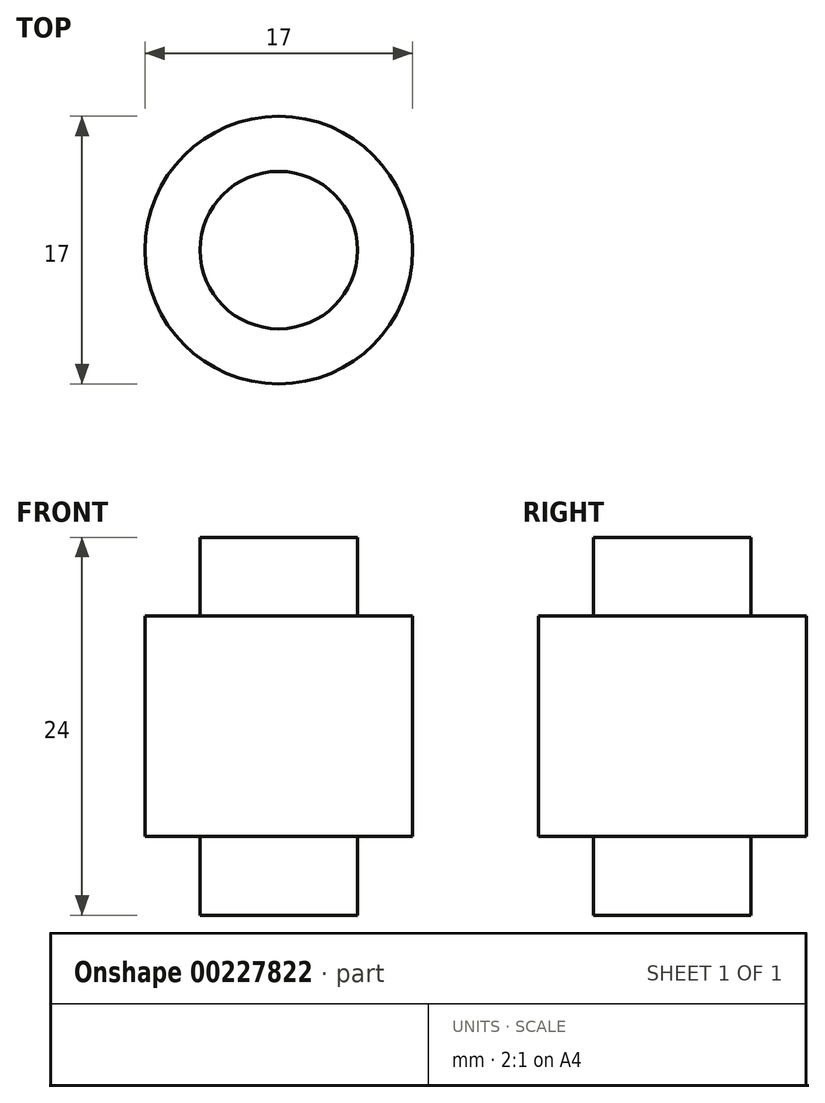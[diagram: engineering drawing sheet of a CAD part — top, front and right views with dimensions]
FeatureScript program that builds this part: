
annotation { "Feature Type Name" : "Feature", "Feature Type Description" : "" }
export const myFeature = defineFeature(function(context is Context, id is Id, definition is map)
    precondition{}
    {
        {
            var Q0;
            Q0=qCreatedBy(makeId("Front.planeOp"),FACE);
            var sketch = newSketch(context, id + "F0", { "sketchPlane" : qUnion([Q0])});
            skLineSegment(sketch, "E0", {"start": v(0, 12) * mm, "end": v(5, 12) * mm});
            skLineSegment(sketch, "E1", {"start": v(5, 12) * mm, "end": v(5, 7) * mm});
            skLineSegment(sketch, "E2", {"start": v(5, 7) * mm, "end": v(8.5, 7) * mm});
            skLineSegment(sketch, "E3", {"start": v(8.5, 7) * mm, "end": v(8.5, 0) * mm});
            skLineSegment(sketch, "E4", {"start": v(0, 25.28) * mm, "end": v(0, -24.24) * mm});
            skLineSegment(sketch, "E5.MirrorCS", {"start": v(5, -7) * mm, "end": v(8.5, -7) * mm});
            skLineSegment(sketch, "E6.MirrorCS", {"start": v(0, -12) * mm, "end": v(5, -12) * mm});
            skLineSegment(sketch, "E7.MirrorCS", {"start": v(8.5, -7) * mm, "end": v(8.5, 0) * mm});
            skLineSegment(sketch, "E8.MirrorCS", {"start": v(5, -12) * mm, "end": v(5, -7) * mm});
            skSolve(sketch);
        }
        {
            var Q0;
            {var subQ0=sQuery(id+"F0.wireOp",EDGE,"E0");Q0=makeQuery(id+"F0.imprint","IMPRINT",FACE,{"disambiguationData":[TD([[makeQuery(id+"F0.imprint","IMPRINT",EDGE,{"derivedFrom":subQ0}),-1.0]])]});}
            var Q1;
            Q1=sQuery(id+"F0.wireOp",EDGE,"E4");
            revolve(context, id + "F1", {"entities" : qUnion([Q0]), "axis" : qUnion([Q1]), "revolveType" : RevolveType.FULL});
        }
    });
